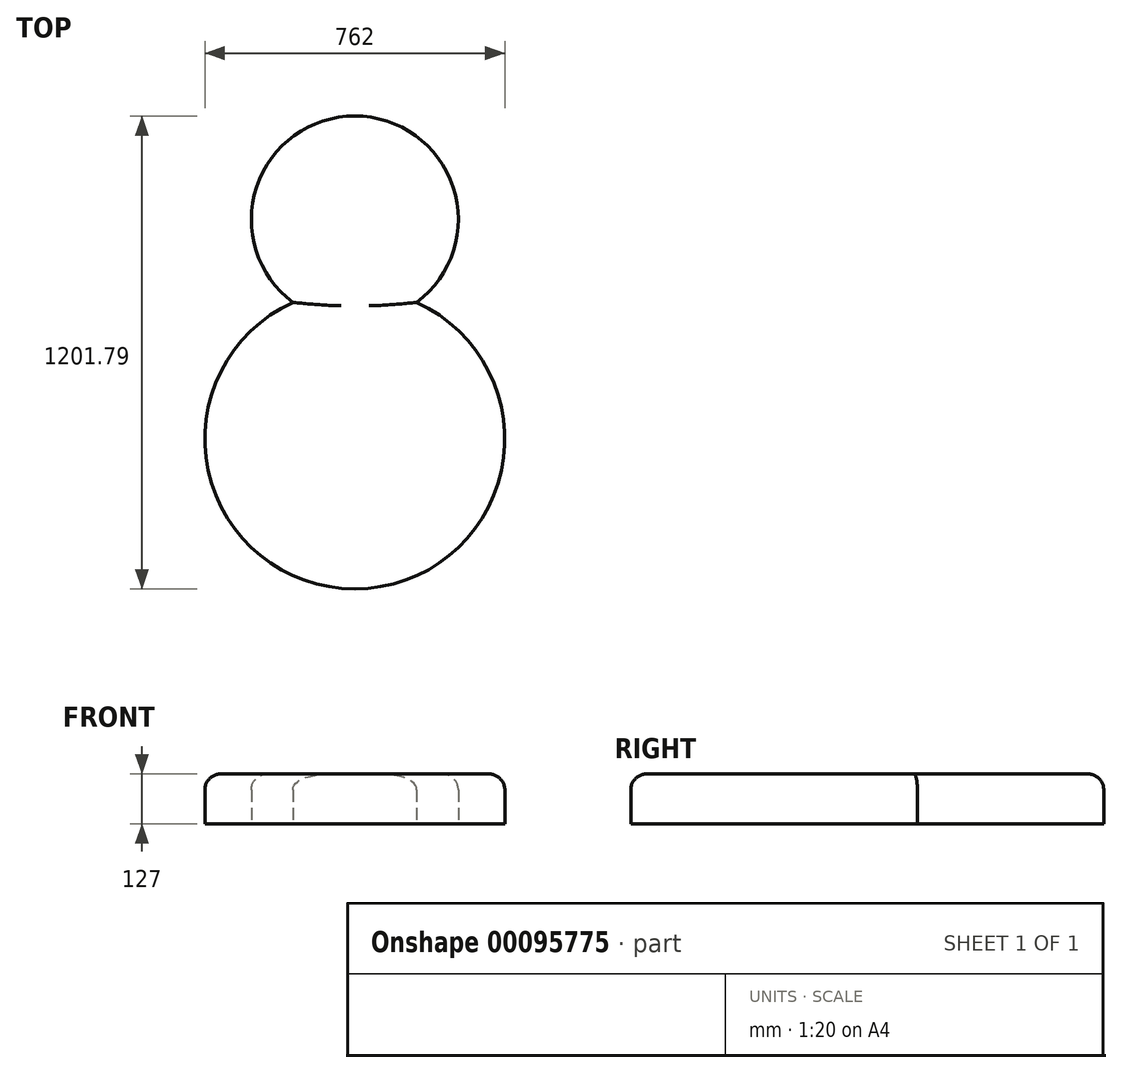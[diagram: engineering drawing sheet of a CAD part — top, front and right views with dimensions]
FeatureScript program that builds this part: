
annotation { "Feature Type Name" : "Feature", "Feature Type Description" : "" }
export const myFeature = defineFeature(function(context is Context, id is Id, definition is map)
    precondition{}
    {
        {
            var Q0;
            Q0=qCreatedBy(makeId("Top.planeOp"),FACE);
            var sketch = newSketch(context, id + "F0", { "sketchPlane" : qUnion([Q0])});
            skArc(sketch, "E0", {"start": v(157.11, 48.52) * mm, "mid": v(0, 522.22) * mm, "end": v(-157.11, 48.52) * mm});
            skArc(sketch, "E1", {"start": v(-157.11, 48.52) * mm, "mid": v(0, -679.57) * mm, "end": v(157.11, 48.52) * mm});
            skSolve(sketch);
        }
        {
            var Q0;
            Q0 = qSketchRegion(id + "F0", true);
            extrude(context, id + "F1", {"entities" : qUnion([Q0]), "depth" : 127 * mm});
        }
        {
            var Q0;
            Q0=makeQuery(id+"F1.opExtrude","CAP_EDGE",EDGE,{"disambiguationData":[OSD([sQuery(id+"F0.wireOp",EDGE,"E0")])],"isStart":false});
            var Q1;
            Q1=makeQuery(id+"F1.opExtrude","CAP_EDGE",EDGE,{"disambiguationData":[OSD([sQuery(id+"F0.wireOp",EDGE,"E1")])],"isStart":false});
            fillet(context, id + "F2", {"entities" : qUnion([Q0, Q1]), "radius" : 40.64 * mm, "tangentPropagation" : true, "allowEdgeOverflow" : false});
        }
    });
